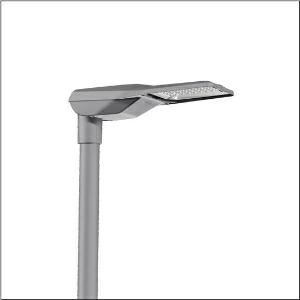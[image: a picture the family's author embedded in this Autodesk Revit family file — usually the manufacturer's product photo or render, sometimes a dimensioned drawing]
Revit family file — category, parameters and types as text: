
# Revit family: streetlight_sl_21_iq_mini___st1_0a_5xe2d31g08hb_3bda
name_source: partatom
category: Lighting Fixtures
units: mm (PartAtom-declared; Revit-internal decimal feet)

## family parameters
Cut with Voids When Loaded = No
Host = Face
Light Source = No
Part Type = Normal
Room Calculation Point = No
Round Connector Dimension = Use Diameter
Shared = No

## types (1)
- --- (1 x LED, 9450 lm, 70.9 W, 3000K)
    Apparent Load = 71 VA
    CIE Flux Codes = 37 72 97 100 100
    Color Rendering = 70
    Color Temperature = 3000K
    Default Elevation = 1800 mm
    Description = Streetlight SL 21 iQ mini, mast luminaire, primary light control with lens, of PMMA, primary optical cover: cover, of toughened safety glass, transparent, light distribution: ST1.0a, light emission: direct distribution, primary light characteristic: asymmetric, installation type: post-top, side-entry, LED, High Power LED, rated luminous flux: 9.450lm, luminous efficacy: 133lm/W, light colour: 730, colour temperature: 3000K, control: Street-Remote, Auto-Match, Temp-Guard, Lumen-Switch, Night-Set, Smart-Wire, Light-Fading, Desk-Remote (wireless, voltage-free reading and setting of iQ features in the workshop via application-optimized NFC function/RFID function), optimised constant luminous flux control (CLO 2.0), presetting dimming linear, mains connection: 220..240V, AC, 50/60Hz, start of lifetime: 71W, end of service life: 75W, reduction: 31W, luminaire housing, of diecast aluminium, powder-coated, Siteco® metallic grey (DB 702S), corrosivity category C5 mid according to DIN EN ISO 12944, please order mast flange separately, inclination adjustable: 0°, 5°, 10°, 15°, sealing non-destructively replaceable, multi-level sealing system, length: 628mm, width: 235mm, height: 110mm, mast flange for spigot size: 42mm (side-entry): 5XC10008XM4, 60/48mm (side-entry/post-top): 5XC10108XM2, 76/60mm (side-entry/post-top): 5XC10108XM1, protection rating (complete): IP66, insulation class (complete): insulation class II (safety insulation), certification: CE, ENEC, ENEC+, VDE, impact resistance: IK09, permissible operating ambient temperature for outdoor applications: -40..+50°C, standard-compliant lighting for roads and squares, packaging unit: 1 piece

Light Distribution: ST1.0a
    Height = 110 mm
    Lamp = 1 x LED
    Lamp Light Flux = 9450 lm
    Lamp Power = 70.9 W
    Lamp count = 1
    Length = 625 mm
    Luminous efficacy = 133 lm/W
    Manufacturer = Siteco
    ModVariant = No
    Model = 5XE2D31G08HB
    Number of Poles = 1
    OnlyDefault = Yes
    Power Factor = 1
    Product Name = Streetlight SL 21 iQ mini | ST1.0a
    Product group = mast luminaire | pylon top
    ProductGroupID = 6100
    Protection Class = Protection class II
    Protection Degree = IP 66
    RLX_Detail_Level = 1
    RLX_Emergency_Light_Flux = 0 lm
    RLX_Emergency_Type = 0
    RLX_Emergency_Type_DB = No
    RlxData = <blob elided: 93237 chars, md5=5b11ccdc>
    Socket = socket
    Standby Power = 0 W
    System Light Flux = 9450 lm
    System Power = 71 W
    Type Comments = factory setting: luminous flux: 100 % | dim-lin: 254 | 711 mA
    Type Image = l_1003519.jpg
    URL = http://relux.com
    VarID = @adj_108309
    Voltage = 0 V
    Weight = 0.00 kg
    Width = 234 mm

## geometry (parser evidence)
native form markers: Blend x4, Sweep x9
no freeform markers — native parametric forms only
